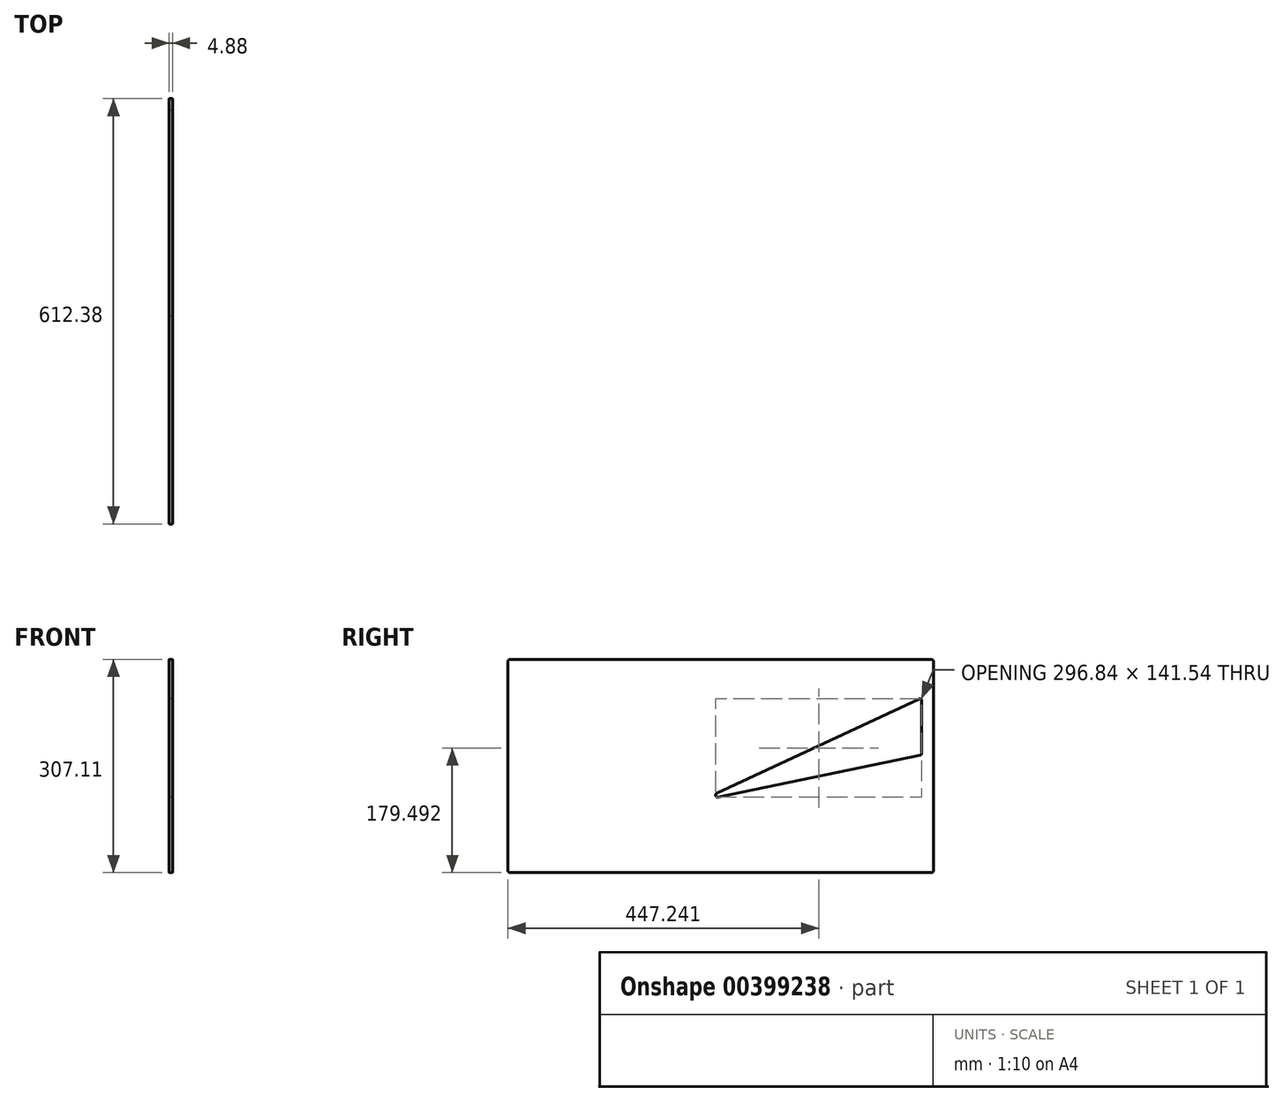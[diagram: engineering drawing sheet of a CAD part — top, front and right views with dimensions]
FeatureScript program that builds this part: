
annotation { "Feature Type Name" : "Feature", "Feature Type Description" : "" }
export const myFeature = defineFeature(function(context is Context, id is Id, definition is map)
    precondition{}
    {
        {
            var Q0;
            Q0=qCreatedBy(makeId("Right.planeOp"),FACE);
            var sketch = newSketch(context, id + "F0", { "sketchPlane" : qUnion([Q0])});
            skLineSegment(sketch, "E0.bottom", {"start": v(7.9, -4.14) * mm, "end": v(58.43, -4.14) * mm});
            skLineSegment(sketch, "E0.top", {"start": v(7.9, 21.45) * mm, "end": v(58.43, 21.45) * mm});
            skLineSegment(sketch, "E0.left", {"start": v(7.65, -3.89) * mm, "end": v(7.65, 21.2) * mm});
            skLineSegment(sketch, "E0.right", {"start": v(58.68, -3.89) * mm, "end": v(58.68, 21.2) * mm});
            skPoint(sketch, "E1.visualSharp", {"position": v(7.65, 21.45) * mm});
            skArc(sketch, "E1.filletArc", {"start": v(7.9, 21.45) * mm, "mid": v(7.73, 21.38) * mm, "end": v(7.65, 21.2) * mm});
            skPoint(sketch, "E2.visualSharp", {"position": v(58.68, 21.45) * mm});
            skArc(sketch, "E2.filletArc", {"start": v(58.68, 21.2) * mm, "mid": v(58.61, 21.38) * mm, "end": v(58.43, 21.45) * mm});
            skPoint(sketch, "E3.visualSharp", {"position": v(58.68, -4.14) * mm});
            skArc(sketch, "E3.filletArc", {"start": v(58.43, -4.14) * mm, "mid": v(58.61, -4.07) * mm, "end": v(58.68, -3.89) * mm});
            skPoint(sketch, "E4.visualSharp", {"position": v(7.65, -4.14) * mm});
            skArc(sketch, "E4.filletArc", {"start": v(7.65, -3.89) * mm, "mid": v(7.73, -4.07) * mm, "end": v(7.9, -4.14) * mm});
            skPoint(sketch, "E5.visualSharp", {"position": v(30.72, 4.47) * mm});
            skPoint(sketch, "E6.visualSharp", {"position": v(57.3, 16.86) * mm});
            skPoint(sketch, "E7.visualSharp", {"position": v(57.3, 4.47) * mm});
            skLineSegment(sketch, "E8", {"start": v(32.7, 5.4) * mm, "end": v(56.93, 16.69) * mm});
            skLineSegment(sketch, "E9", {"start": v(57.09, 9.96) * mm, "end": v(32.86, 4.92) * mm});
            skLineSegment(sketch, "E10", {"start": v(57.3, 16.46) * mm, "end": v(57.3, 10.2) * mm});
            skArc(sketch, "E11.filletArc", {"start": v(32.7, 5.4) * mm, "mid": v(32.57, 5.09) * mm, "end": v(32.86, 4.92) * mm});
            skArc(sketch, "E12.filletArc", {"start": v(57.3, 16.46) * mm, "mid": v(57.17, 16.67) * mm, "end": v(56.93, 16.69) * mm});
            skPoint(sketch, "E13.visualSharp", {"position": v(57.3, 10) * mm});
            skArc(sketch, "E13.filletArc", {"start": v(57.09, 9.96) * mm, "mid": v(57.23, 10.04) * mm, "end": v(57.3, 10.2) * mm});
            skSolve(sketch);
        }
        {
            var Q0;
            Q0 = qSketchRegion(id + "F0", true);
            extrude(context, id + "F1", {"entities" : qUnion([Q0]), "endBound" : BoundingType.SYMMETRIC, "depth" : 0.4 * mm});
        }
        {
            var Q0;
            Q0=makeQuery(id+"F1.opExtrude","SWEPT_BODY",BODY,{"disambiguationData":[OSD([sQuery(id+"F0.wireOp",EDGE,"E0.bottom"),sQuery(id+"F0.wireOp",EDGE,"E0.top"),sQuery(id+"F0.wireOp",EDGE,"E0.left"),sQuery(id+"F0.wireOp",EDGE,"E0.right"),sQuery(id+"F0.wireOp",EDGE,"E1.filletArc"),sQuery(id+"F0.wireOp",EDGE,"E2.filletArc"),sQuery(id+"F0.wireOp",EDGE,"E3.filletArc"),sQuery(id+"F0.wireOp",EDGE,"E4.filletArc"),sQuery(id+"F0.wireOp",EDGE,"E8"),sQuery(id+"F0.wireOp",EDGE,"E9"),sQuery(id+"F0.wireOp",EDGE,"E10"),sQuery(id+"F0.wireOp",EDGE,"E11.filletArc"),sQuery(id+"F0.wireOp",EDGE,"E12.filletArc"),sQuery(id+"F0.wireOp",EDGE,"E13.filletArc")])]});
            var Q1;
            Q1=qCreatedBy(makeId("Origin.pointOp"),VERTEX);
            transform(context, id + "F2", {"entities" : qUnion([Q0]), "transformType" : TransformType.SCALE_UNIFORMLY, "scale" : 12, "scalePoint" : qUnion([Q1]), "makeCopy" : false});
        }
    });
